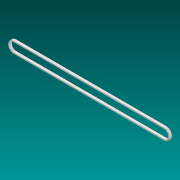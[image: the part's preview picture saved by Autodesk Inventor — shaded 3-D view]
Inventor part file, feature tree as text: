
AUTODESK INVENTOR PART (.ipt)
format: ipt  version: 2021 (Build 250183000, 183)  size: 86,528 bytes
history: native  units: mm
features: extrude x1, sketch x1
ambient origin geometry x8: Origin, YZ Plane, XZ Plane, XY Plane, X Axis, Y Axis, Z Axis, Center Point
bodies: 实体1 (feature_tree)
feature tree (2):
  extrude  "拉伸1"  Depth=36.0mm
  sketch  "草图1"  dims[d0=36.0mm d1=36.0mm d2=576.0mm d3=5.0mm d4=10.0mm d5=0.0mm]
